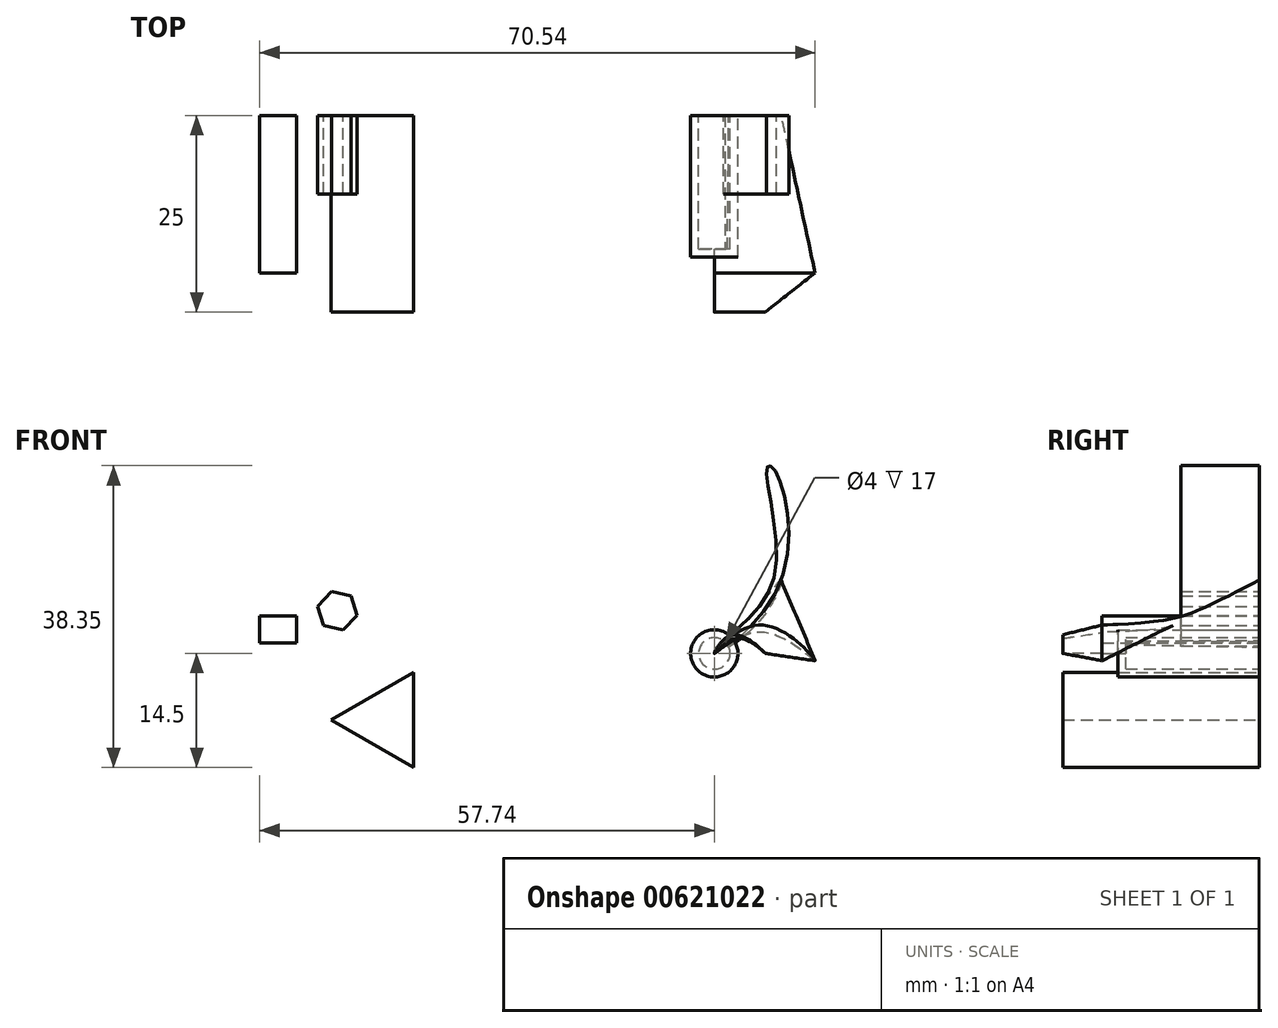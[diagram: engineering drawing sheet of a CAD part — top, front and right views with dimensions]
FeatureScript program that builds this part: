
annotation { "Feature Type Name" : "Feature", "Feature Type Description" : "" }
export const myFeature = defineFeature(function(context is Context, id is Id, definition is map)
    precondition{}
    {
        {
            var Q0;
            Q0=qCreatedBy(makeId("Front.planeOp"),FACE);
            var sketch = newSketch(context, id + "F0", { "sketchPlane" : qUnion([Q0])});
            skCircle(sketch, "E0", {"center": v(0, 0) * mm, "radius": 25 * mm});
            skSolve(sketch);
        }
        {
            var Q0;
            Q0=qCreatedBy(makeId("Front.planeOp"),FACE);
            var sketch = newSketch(context, id + "F1", { "sketchPlane" : qUnion([Q0])});
            skCircle(sketch, "E1.cCircle", {"center": v(-47.89, 5.42) * mm, "radius": 2.22 * mm, "construction": true});
            skLineSegment(sketch, "E1.0", {"start": v(-45.38, 4.84) * mm, "end": v(-47.14, 2.96) * mm});
            skLineSegment(sketch, "E1.1", {"start": v(-47.14, 2.96) * mm, "end": v(-49.64, 3.54) * mm});
            skLineSegment(sketch, "E1.2", {"start": v(-49.64, 3.54) * mm, "end": v(-50.39, 6) * mm});
            skLineSegment(sketch, "E1.3", {"start": v(-50.39, 6) * mm, "end": v(-48.63, 7.87) * mm});
            skLineSegment(sketch, "E1.4", {"start": v(-48.63, 7.87) * mm, "end": v(-46.13, 7.3) * mm});
            skLineSegment(sketch, "E1.5", {"start": v(-46.13, 7.3) * mm, "end": v(-45.38, 4.84) * mm});
            skPoint(sketch, "E1.0.midPoint", {"position": v(-46.26, 3.9) * mm});
            skSolve(sketch);
        }
        {
            var Q0;
            Q0=qSketchRegion(id+"F1",true);
            extrude(context, id + "F2", {"entities" : qUnion([Q0]), "depth" : 10 * mm, "offsetDistance" : 25 * mm});
        }
        {
            var Q0;
            Q0=qCreatedBy(makeId("Front.planeOp"),FACE);
            var sketch = newSketch(context, id + "F3", { "sketchPlane" : qUnion([Q0])});
            skLineSegment(sketch, "E2.bottom", {"start": v(-57.74, 4.77) * mm, "end": v(-53.09, 4.77) * mm});
            skLineSegment(sketch, "E2.top", {"start": v(-57.74, 1.3) * mm, "end": v(-53.09, 1.3) * mm});
            skLineSegment(sketch, "E2.left", {"start": v(-57.74, 4.77) * mm, "end": v(-57.74, 1.3) * mm});
            skLineSegment(sketch, "E2.right", {"start": v(-53.09, 4.77) * mm, "end": v(-53.09, 1.3) * mm});
            skSolve(sketch);
        }
        {
            var Q0;
            Q0=makeQuery(id+"F3.imprint","IMPRINT",FACE,{"disambiguationData":[TD([[makeQuery(id+"F3.imprint","IMPRINT",EDGE,{"derivedFrom":sQuery(id+"F3.wireOp",EDGE,"E2.bottom")}),-1.0]])]});
            extrude(context, id + "F4", {"entities" : qUnion([Q0]), "depth" : 20 * mm, "offsetDistance" : 25 * mm});
        }
        {
            var Q0;
            Q0=qCreatedBy(makeId("Front.planeOp"),FACE);
            var sketch = newSketch(context, id + "F5", { "sketchPlane" : qUnion([Q0])});
            skFitSpline(sketch, "E3", {"points": [v(0, 0) * mm, v(8.43, 9.16) * mm, v(7.39, 23.63) * mm, v(6.7, 23.63) * mm, v(7.62, 9.85) * mm, v(1.02, 1.52) * mm, v(0, 0) * mm]});
            skSolve(sketch);
        }
        {
            var Q0;
            Q0=qSketchRegion(id+"F5",true);
            extrude(context, id + "F6", {"entities" : qUnion([Q0]), "depth" : 10 * mm, "offsetDistance" : 25 * mm});
        }
        {
            var Q0;
            Q0=qCreatedBy(makeId("Front.planeOp"),FACE);
            var sketch = newSketch(context, id + "F7", { "sketchPlane" : qUnion([Q0])});
            skFitSpline(sketch, "E4", {"points": [v(0, 0) * mm, v(4.66, 4.78) * mm, v(8.48, 9.3) * mm, v(5.47, 3.8) * mm, v(0, 0) * mm]});
            skSolve(sketch);
        }
        {
            var Q0;
            Q0=makeQuery(id+"F4.opExtrude","CAP_FACE",FACE,{"disambiguationData":[OSD([sQuery(id+"F3.wireOp",EDGE,"E2.bottom"),sQuery(id+"F3.wireOp",EDGE,"E2.top"),sQuery(id+"F3.wireOp",EDGE,"E2.left"),sQuery(id+"F3.wireOp",EDGE,"E2.right")])],"isStart":false});
            var sketch = newSketch(context, id + "F8", { "sketchPlane" : qUnion([Q0])});
            skFitSpline(sketch, "E5", {"points": [v(0, 0) * mm, v(5.93, 3.6) * mm, v(12.8, -0.92) * mm, v(5.88, 2.68) * mm, v(0, 0) * mm]});
            skSolve(sketch);
        }
        {
            var Q1;
            Q1=qSketchRegion(id+"F7",true);
            var Q2;
            Q2=qSketchRegion(id+"F8",true);
            loft(context, id + "F9", {"sheetProfilesArray" : [{ "sheetProfileEntities" : qUnion([Q1]) }, { "sheetProfileEntities" : qUnion([Q2]) }]});
        }
        {
            var Q0;
            Q0=makeQuery(id+"F0.imprint","IMPRINT",FACE,{"disambiguationData":[TD([[makeQuery(id+"F0.imprint","IMPRINT",EDGE,{"derivedFrom":sQuery(id+"F0.wireOp",EDGE,"E0")}),1.0]])]});
            extrude(context, id + "F10", {"entities" : qUnion([Q0]), "oppositeDirection" : true, "depth" : 2 * mm, "offsetDistance" : 25 * mm});
        }
        {
            var Q0;
            Q0=qCreatedBy(makeId("Front.planeOp"),FACE);
            var sketch = newSketch(context, id + "F11", { "sketchPlane" : qUnion([Q0])});
            skCircle(sketch, "E6", {"center": v(0, 0) * mm, "radius": 2 * mm});
            skSolve(sketch);
        }
        {
            var Q0;
            Q0=qCreatedBy(makeId("Front.planeOp"),FACE);
            var sketch = newSketch(context, id + "F12", { "sketchPlane" : qUnion([Q0])});
            skCircle(sketch, "E7", {"center": v(0, 0) * mm, "radius": 3 * mm});
            skSolve(sketch);
        }
        {
            var Q0;
            Q0 = qSketchRegion(id + "F12", true);
            extrude(context, id + "F13", {"entities" : qUnion([Q0]), "depth" : 18 * mm, "offsetDistance" : 25 * mm});
        }
        {
            var Q0;
            Q0 = qSketchRegion(id + "F11", true);
            extrude(context, id + "F14", {"entities" : qUnion([Q0]), "operationType" : NewBodyOperationType.REMOVE, "depth" : 17 * mm, "offsetDistance" : 25 * mm, "hasSecondDirection" : true, "secondDirectionOppositeDirection" : true, "secondDirectionDepth" : 5 * mm});
        }
        {
            var Q0;
            Q0=makeQuery(id+"F10.opExtrude","SWEPT_BODY",BODY,{"disambiguationData":[OSD([sQuery(id+"F0.wireOp",EDGE,"E0")])]});
            deleteBodies(context, id + "F15", {"entities" : qUnion([Q0])});
        }
        {
            var Q0;
            Q0=qCreatedBy(makeId("Front.planeOp"),FACE);
            var sketch = newSketch(context, id + "F16", { "sketchPlane" : qUnion([Q0])});
            skCircle(sketch, "E8.cCircle", {"center": v(-41.72, -8.46) * mm, "radius": 3.49 * mm, "construction": true});
            skLineSegment(sketch, "E8.0", {"start": v(-38.23, -2.41) * mm, "end": v(-38.23, -14.5) * mm});
            skLineSegment(sketch, "E8.1", {"start": v(-38.23, -14.5) * mm, "end": v(-48.7, -8.46) * mm});
            skLineSegment(sketch, "E8.2", {"start": v(-48.7, -8.46) * mm, "end": v(-38.23, -2.41) * mm});
            skPoint(sketch, "E8.0.midPoint", {"position": v(-38.23, -8.46) * mm});
            skSolve(sketch);
        }
        {
            var Q0;
            Q0=makeQuery(id+"F16.imprint","IMPRINT",FACE,{"disambiguationData":[TD([[makeQuery(id+"F16.imprint","IMPRINT",EDGE,{"derivedFrom":sQuery(id+"F16.wireOp",EDGE,"E8.0")}),-1.0]])]});
            extrude(context, id + "F17", {"entities" : qUnion([Q0]), "depth" : 25 * mm, "offsetDistance" : 25 * mm});
        }
        {
            var Q0;
            Q0=makeQuery(id+"F17.opExtrude","CAP_FACE",FACE,{"disambiguationData":[OSD([sQuery(id+"F16.wireOp",EDGE,"E8.0"),sQuery(id+"F16.wireOp",EDGE,"E8.1"),sQuery(id+"F16.wireOp",EDGE,"E8.2")])],"isStart":false});
            var sketch = newSketch(context, id + "F18", { "sketchPlane" : qUnion([Q0])});
            skFitSpline(sketch, "E9", {"points": [v(0, 0) * mm, v(2.44, 2.36) * mm, v(6.47, 0) * mm, v(2.89, 1.91) * mm, v(0, 0) * mm]});
            skSolve(sketch);
        }
        {
            var Q1;
            Q1=makeQuery(id+"F9.opLoft","CAP_FACE",FACE,{"disambiguationData":[OSD([makeQuery(id+"F8.imprint","IMPRINT",FACE,{"disambiguationData":[TD([[makeQuery(id+"F8.imprint","IMPRINT",EDGE,{"derivedFrom":sQuery(id+"F8.wireOp",EDGE,"E5")}),-1.0]])]})])],"isStart":true});
            var Q2;
            Q2=makeQuery(id+"F18.imprint","IMPRINT",FACE,{"disambiguationData":[TD([[makeQuery(id+"F18.imprint","IMPRINT",EDGE,{"derivedFrom":sQuery(id+"F18.wireOp",EDGE,"E9")}),-1.0]])]});
            loft(context, id + "F19", {"sheetProfilesArray" : [{ "sheetProfileEntities" : qUnion([Q1]) }, { "sheetProfileEntities" : qUnion([Q2]) }]});
        }
    });
